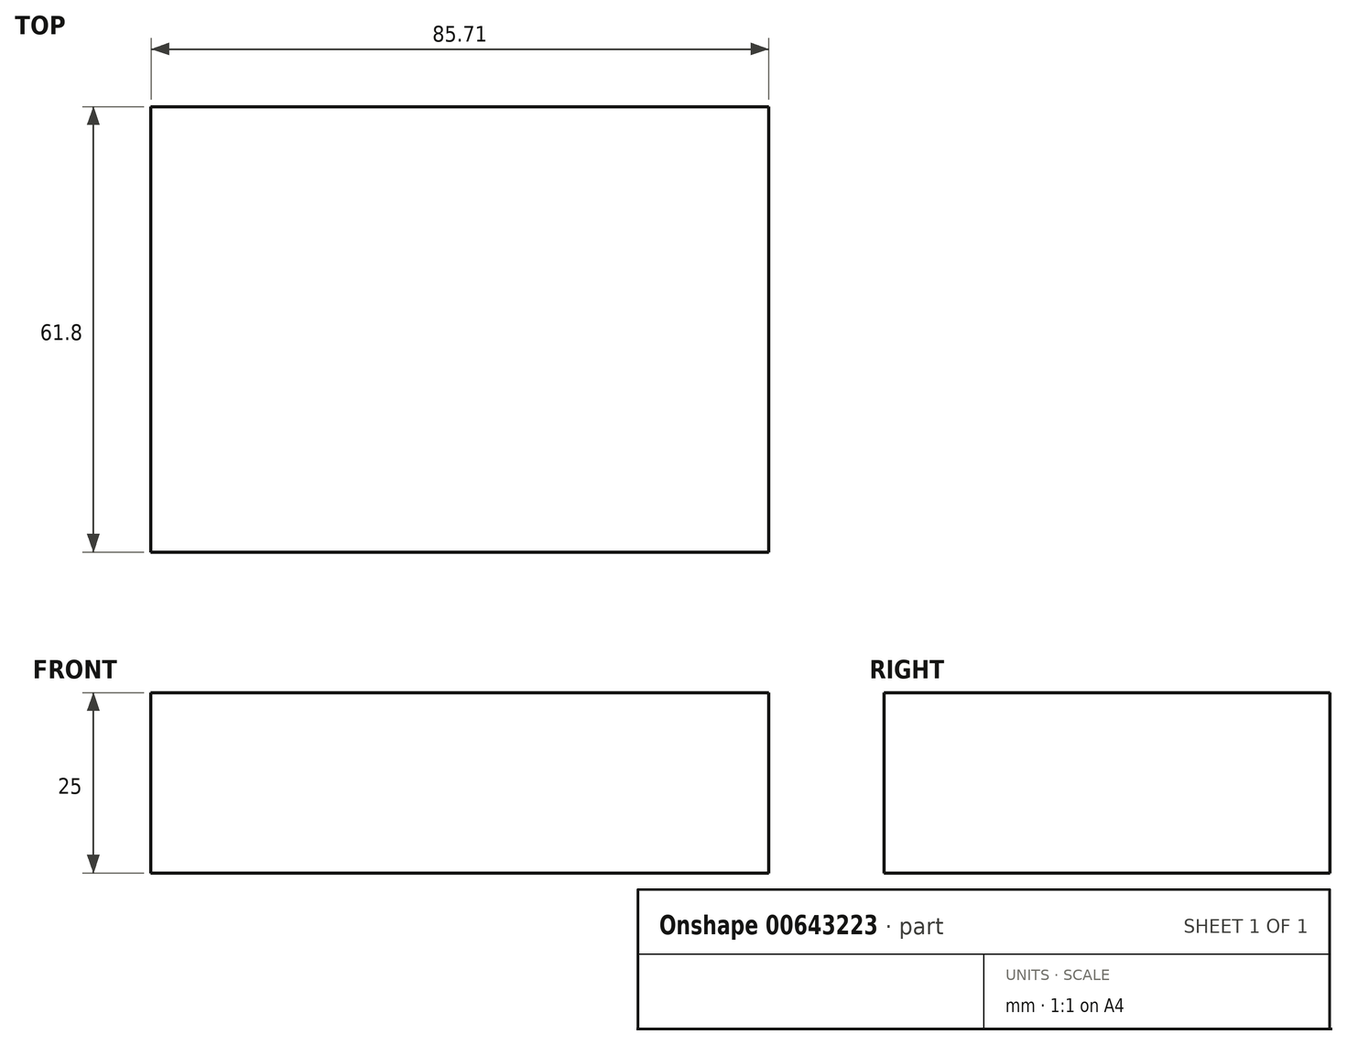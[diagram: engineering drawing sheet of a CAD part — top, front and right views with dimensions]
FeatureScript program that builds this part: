
annotation { "Feature Type Name" : "Feature", "Feature Type Description" : "" }
export const myFeature = defineFeature(function(context is Context, id is Id, definition is map)
    precondition{}
    {
        {
            var Q0;
            Q0=qCreatedBy(makeId("Top.planeOp"),FACE);
            var sketch = newSketch(context, id + "F0", { "sketchPlane" : qUnion([Q0])});
            skLineSegment(sketch, "E0.bottom", {"start": v(-39.1, 27.8) * mm, "end": v(46.62, 27.8) * mm});
            skLineSegment(sketch, "E0.top", {"start": v(-39.1, -33.99) * mm, "end": v(46.62, -33.99) * mm});
            skLineSegment(sketch, "E0.left", {"start": v(-39.1, 27.8) * mm, "end": v(-39.1, -33.99) * mm});
            skLineSegment(sketch, "E0.right", {"start": v(46.62, 27.8) * mm, "end": v(46.62, -33.99) * mm});
            skSolve(sketch);
        }
        {
            var Q0;
            Q0=makeQuery(id+"F0.imprint","IMPRINT",FACE,{"disambiguationData":[TD([[makeQuery(id+"F0.imprint","IMPRINT",EDGE,{"derivedFrom":sQuery(id+"F0.wireOp",EDGE,"E0.bottom")}),-1.0]])]});
            extrude(context, id + "F1", {"entities" : qUnion([Q0]), "depth" : 25 * mm, "offsetDistance" : 25 * mm});
        }
    });
